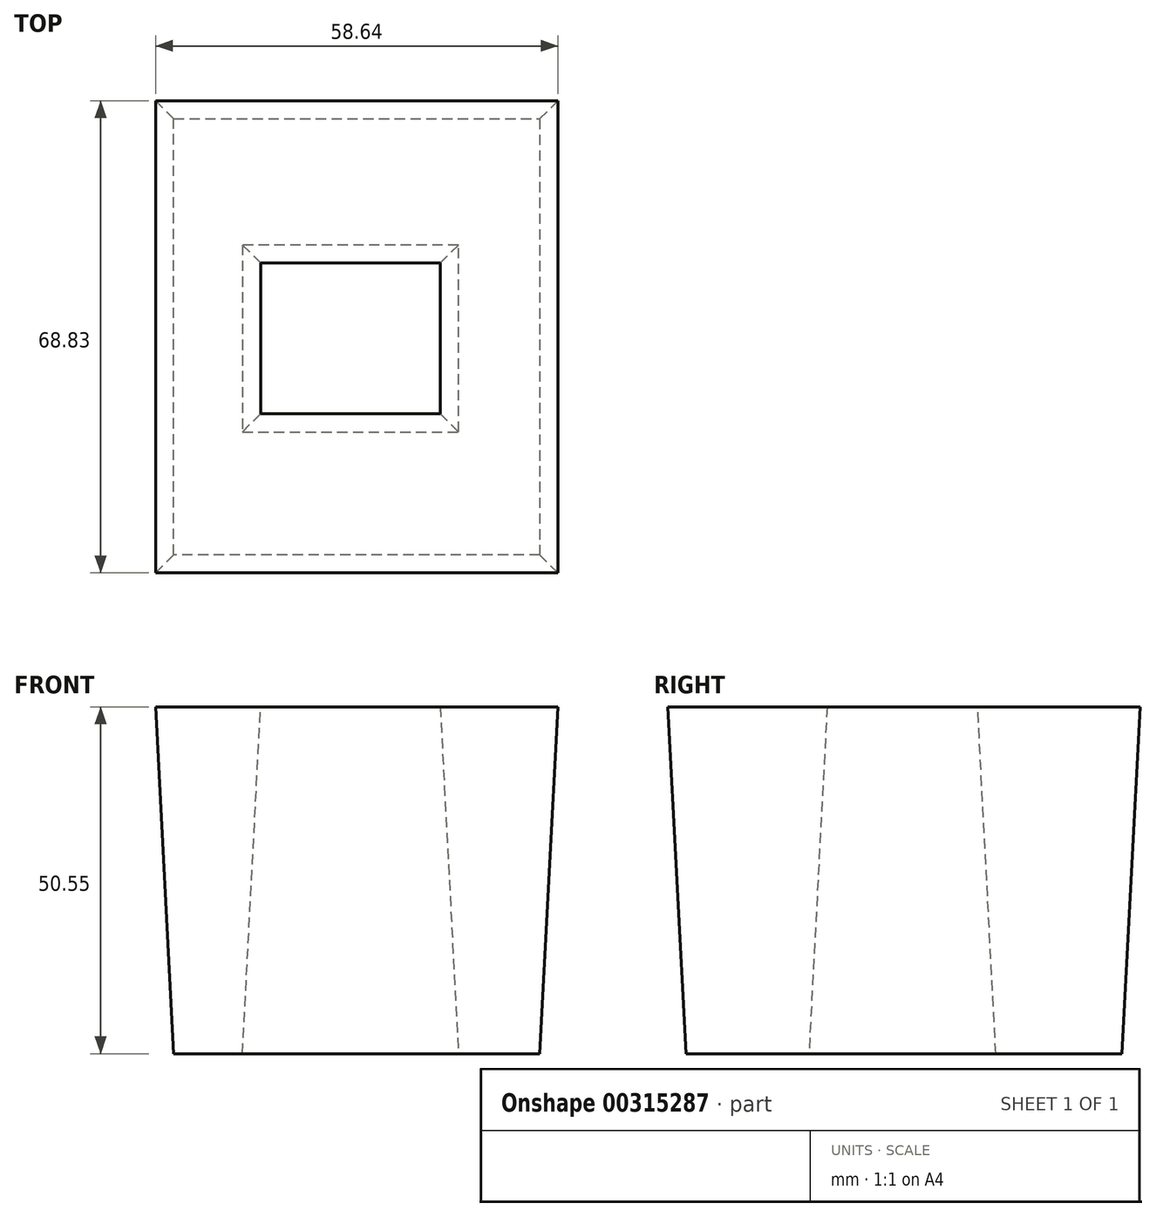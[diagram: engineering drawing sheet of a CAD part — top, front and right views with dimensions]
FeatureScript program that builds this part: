
annotation { "Feature Type Name" : "Feature", "Feature Type Description" : "" }
export const myFeature = defineFeature(function(context is Context, id is Id, definition is map)
    precondition{}
    {
        {
            var Q0;
            Q0=qCreatedBy(makeId("Top.planeOp"),FACE);
            var sketch = newSketch(context, id + "F0", { "sketchPlane" : qUnion([Q0])});
            skLineSegment(sketch, "E0.bottom", {"start": v(-60.81, -58.3) * mm, "end": v(-7.5, -58.3) * mm});
            skLineSegment(sketch, "E0.top", {"start": v(-60.81, 5.2) * mm, "end": v(-7.5, 5.2) * mm});
            skLineSegment(sketch, "E0.left", {"start": v(-60.81, -58.3) * mm, "end": v(-60.81, 5.2) * mm});
            skLineSegment(sketch, "E0.right", {"start": v(-7.5, -58.3) * mm, "end": v(-7.5, 5.2) * mm});
            skLineSegment(sketch, "E1.bottom", {"start": v(-50.83, -13.16) * mm, "end": v(-19.34, -13.16) * mm});
            skLineSegment(sketch, "E1.top", {"start": v(-50.83, -40.42) * mm, "end": v(-19.34, -40.42) * mm});
            skLineSegment(sketch, "E1.left", {"start": v(-50.83, -13.16) * mm, "end": v(-50.83, -40.42) * mm});
            skLineSegment(sketch, "E1.right", {"start": v(-19.34, -13.16) * mm, "end": v(-19.34, -40.42) * mm});
            skCircle(sketch, "E2", {"center": v(-35.08, -25.65) * mm, "radius": 9.35 * mm});
            skPoint(sketch, "E2.centerSnap0", {"position": v(-35.08, -40.42) * mm});
            skSolve(sketch);
        }
        {
            var Q0;
            Q0=makeQuery(id+"F0.imprint","IMPRINT",FACE,{"disambiguationData":[TD([[makeQuery(id+"F0.imprint","IMPRINT",EDGE,{"derivedFrom":sQuery(id+"F0.wireOp",EDGE,"E0.bottom")}),1.0]])]});
            extrude(context, id + "F1", {"entities" : qUnion([Q0]), "depth" : 50.8 * mm, "hasDraft" : true, "draftAngle" : 3 * degree, "hasSecondDirection" : true, "secondDirectionOppositeDirection" : false, "secondDirectionDepth" : 0.25 * mm});
        }
    });
